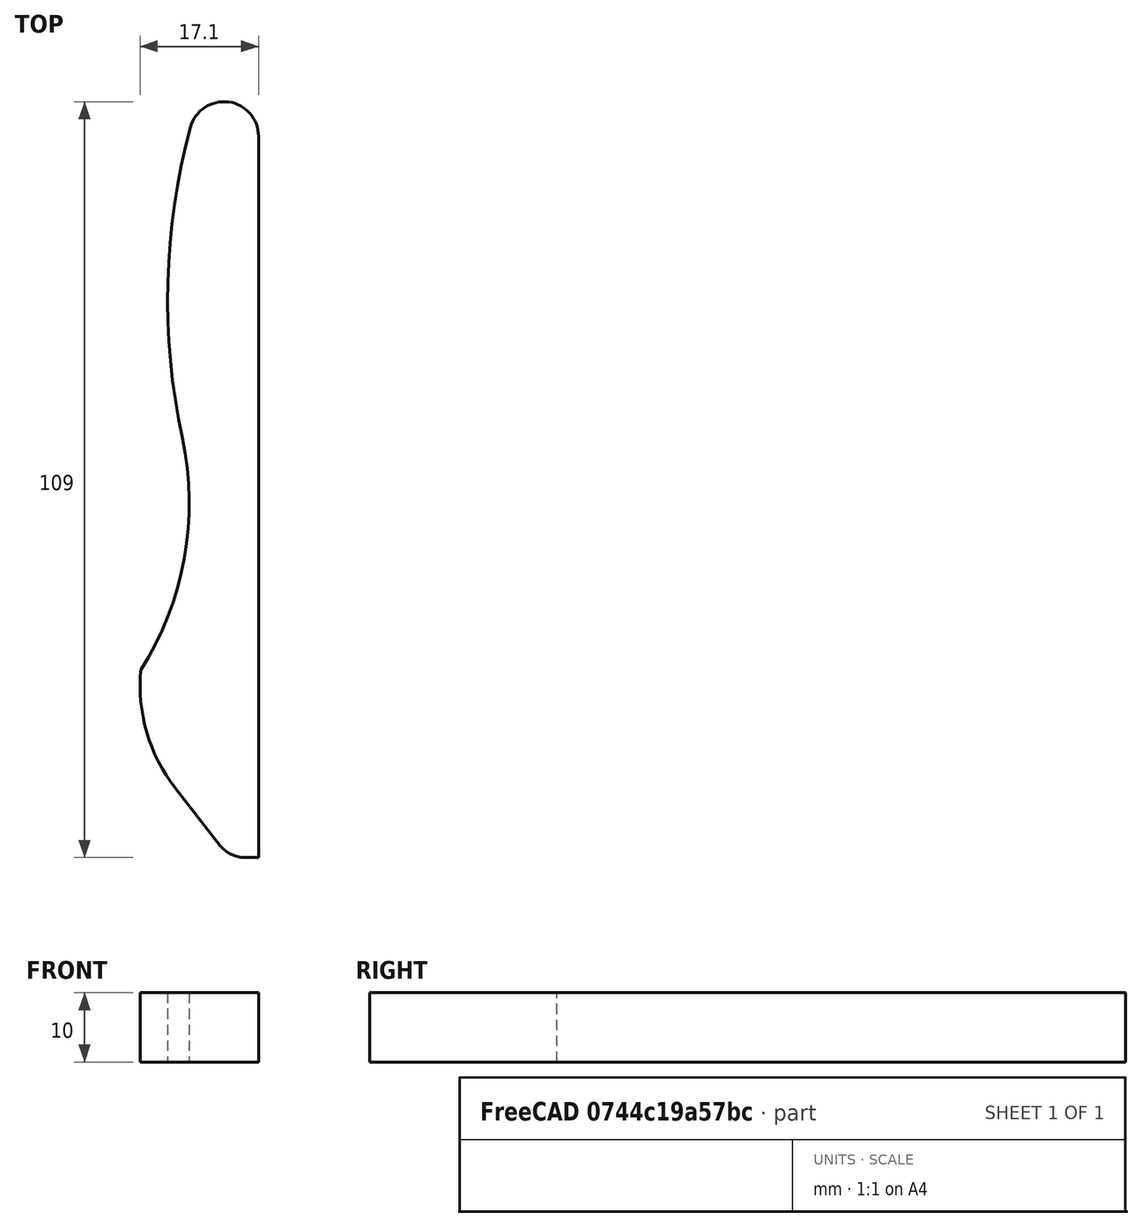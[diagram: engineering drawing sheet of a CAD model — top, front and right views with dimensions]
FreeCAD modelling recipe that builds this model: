
FCSTD DOCUMENT  (FreeCAD 0.19R23756 (Git))
Label: CLAMP_3
License: All rights reserved
LicenseURL: http://en.wikipedia.org/wiki/All_rights_reserved
objects: Sketcher::SketchObject×1, PartDesign::Pad×1, PartDesign::Body×1
note: 4 computed .brp shape members not serialized (recipe doc carries the construction recipe); baked Part::Feature solids carry a one-line shape summary decoded from their .brp

FEATURE [Sketcher::SketchObject] Sketch
  FullyConstrained = true
  MapMode = 5
  Support = -> [XY_Plane]
  sketch-geometry (8):
    g0: LineSegment StartX=0 StartY=0 StartZ=0 EndX=0 EndY=-104 EndZ=0
    g1: LineSegment StartX=0 StartY=-104 StartZ=0 EndX=-2 EndY=-104 EndZ=0
    g2: ArcOfCircle CenterX=-2 CenterY=-99.5 CenterZ=0 NormalX=0 NormalY=0 NormalZ=1 AngleXU=0 Radius=4.5 StartAngle=3.80424 EndAngle=4.71239
    g3: LineSegment StartX=-5.54764 StartY=-102.268 StartZ=0 EndX=-12 EndY=-94 EndZ=0
    g4: ArcOfCircle CenterX=6.99318 CenterY=-79.1785 CenterZ=0 NormalX=0 NormalY=0 NormalZ=1 AngleXU=0 Radius=24.0919 StartAngle=3.05105 EndAngle=3.80424
    g5: ArcOfCircle CenterX=-55.014 CenterY=-52.9181 CenterZ=0 NormalX=0 NormalY=0 NormalZ=1 AngleXU=0 Radius=45 StartAngle=5.7185 EndAngle=6.49291
    g6: ArcOfCircle CenterX=82.8964 CenterY=-23.563 CenterZ=0 NormalX=0 NormalY=0 NormalZ=1 AngleXU=0 Radius=96 StartAngle=2.87967 EndAngle=3.35132
    g7: ArcOfCircle CenterX=-5 CenterY=-6e-16 CenterZ=0 NormalX=0 NormalY=0 NormalZ=1 AngleXU=0 Radius=5 StartAngle=1e-16 EndAngle=2.87967
  constraints (22):
    c: Coincident(g-1,g0)
    c: PointOnObject(g0,g-2)
    c: Coincident(g0,g1)
    c: Tangent(g1,g2) = 1.5708
    c: Tangent(g2,g3) = 1.5708
    c: Tangent(g3,g4) = 1.5708
    c: DistanceY(g0) = -104
    c: Horizontal(g1)
    c: DistanceX(g1,g1) = 2
    c: Radius(g2) = 4.5
    c: DistanceX(g3) = -12
    c: DistanceY(g3) = -94
    c: DistanceX(g4) = -17
    c: DistanceY(g4) = -77
    c: Coincident(g5,g4)
    c: Radius(g7) = 5
    c: Radius(g6) = 96
    c: Radius(g5) = 45
    c: Tangent(g7,g0) = 1.5708
    c: Tangent(g7,g6) = -1.5708
    c: Tangent(g6,g5) = 1.5708
    c: DistanceX(g5,g7) = 6
FEATURE [PartDesign::Pad] Pad
  AllowMultiFace = false
  Direction = (1,1,1)
  Length = 10
  Length2 = 100
  Profile = -> Sketch
  Type = 0
FEATURE [PartDesign::Body] Body
  Group = -> [Sketch,Pad]
  Origin = -> Origin
  Tip = -> Pad
